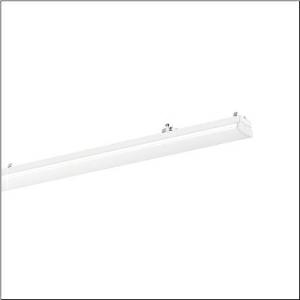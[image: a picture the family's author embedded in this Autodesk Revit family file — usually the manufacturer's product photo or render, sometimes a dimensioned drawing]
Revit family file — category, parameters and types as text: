
# Revit family: licross_r__11_recessed_opal_mo_51te1d7n46xg_ba74
name_source: partatom
category: Lighting Fixtures
units: mm (PartAtom-declared; Revit-internal decimal feet)

## family parameters
Cut with Voids When Loaded = No
Host = Face
Light Source = No
Part Type = Normal
Room Calculation Point = No
Round Connector Dimension = Use Diameter
Shared = No

## types (1)
- Licross® 11 recessed opal MO (1 x LED, 6300 lm, 35.1 W, 4000K)
    Apparent Load = 35 VA
    CIE Flux Codes = 44 73 91 87 100
    Color Rendering = 80
    Color Temperature = 4000K
    Default Elevation = 1800 mm
    Description = Licross® 11 recessed opal MO, luminaire insert, of sheet steel, coil coated, white, length: 1.500mm, width: 76mm, height: 87mm, LED rated luminous flux: 6.300lm, light colour: 840, control gear: ON/OFF, with plug, 3-pole, with phase selection, mains connection: 220..240V, AC, 50/60Hz, rated input power: 35W, internal wiring halogen-free, primary optical cover: cover, of PMMA, light emission: direct with ceiling illumination distribution, primary light characteristic: symmetric, protection rating (complete): IP54, insulation class (complete): insulation class I (protective earthing), certification: CE, ENEC, VDE, UKCA, protection symbol: D if used in an environment with non-conductive dust loads with corresponding accessories, impact resistance: IK06, permissible ambient temperature for indoor applications: -35..+45°C, corresponds to IFS (International Featured Standards) requirements for safety and quality in the food industry, reducing of maximum allowable ambient temperature of 5°C with ceiling mounting, packaging unit: 1 piece
    Height = 83 mm
    Lamp = 1 x LED
    Lamp Light Flux = 6300 lm
    Lamp Power = 35.1 W
    Lamp count = 1
    Length = 1500 mm
    Luminous efficacy = 179 lm/W
    Manufacturer = Siteco
    ModVariant = No
    Model = 51TE1D7N46XG
    Mounting Place = Ceiling
    Mounting Type = Pendant
    Number of Poles = 1
    OnlyDefault = Yes
    Power Factor = 1
    Product Name = Licross® 11 recessed opal MO
    Product group = luminaire insert | ceiling pendant
    ProductGroupID = 902
    Protection Class = Protection class I
    Protection Degree = IP 54
    RLX_Detail_Level = 1
    RLX_Emergency_Light_Flux = 0 lm
    RLX_Emergency_Type = 0
    RLX_Emergency_Type_DB = No
    RlxData = <blob elided: 23089 chars, md5=45937682>
    Socket = socket
    Standby Power = 0 W
    System Light Flux = 6300 lm
    System Power = 35 W
    Type Comments = Product without accessories
    Type Image = l_1313666.jpg
    URL = http://relux.com
    VarID = ---
    Voltage = 0 V
    Weight = 0.00 kg
    Width = 76 mm

## geometry (parser evidence)
native form markers: Blend x4, Sweep x14
no freeform markers — native parametric forms only
